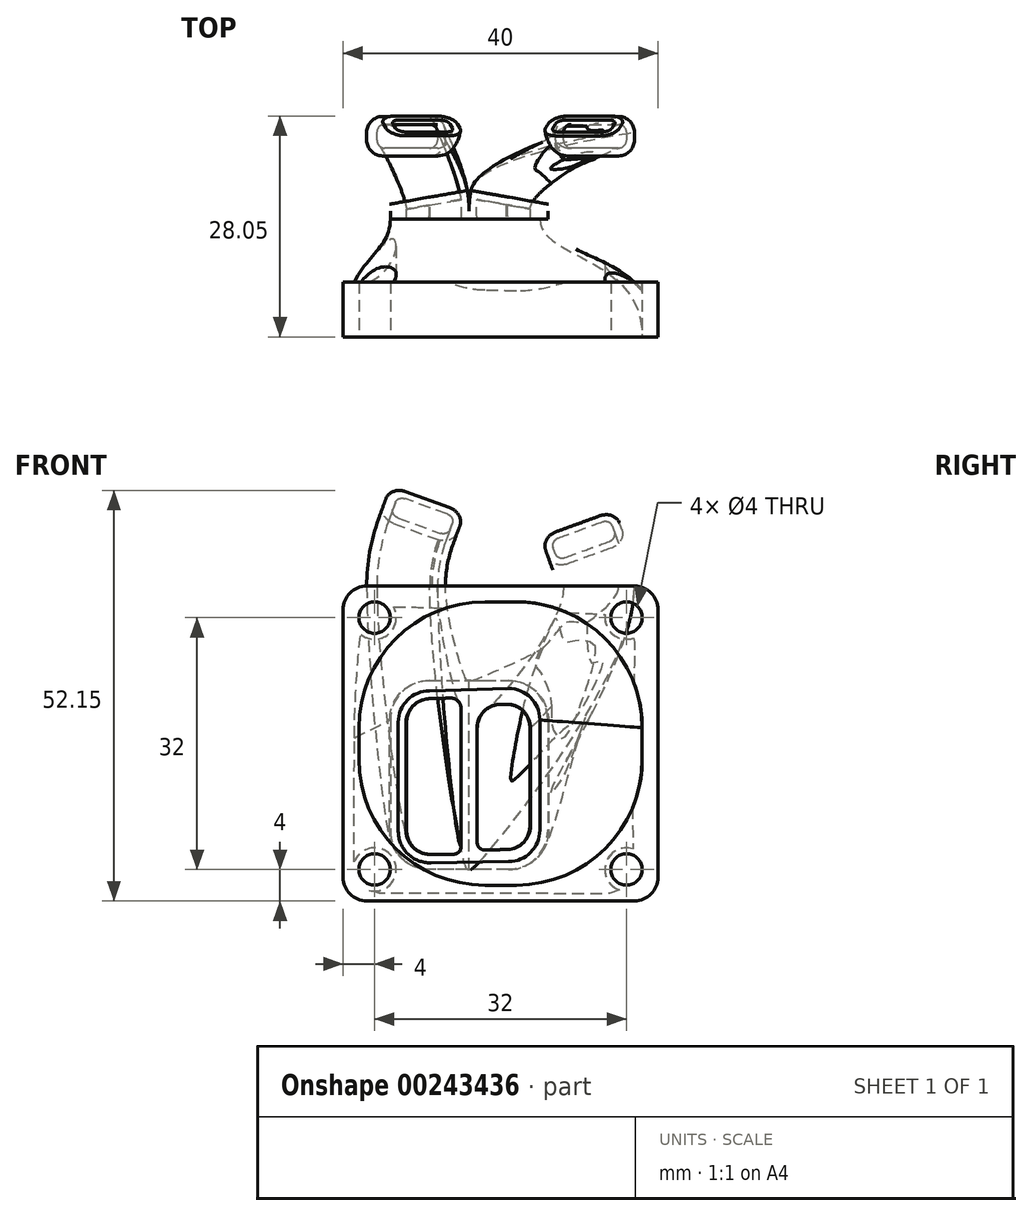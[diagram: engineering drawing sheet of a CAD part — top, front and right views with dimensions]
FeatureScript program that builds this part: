
annotation { "Feature Type Name" : "Feature", "Feature Type Description" : "" }
export const myFeature = defineFeature(function(context is Context, id is Id, definition is map)
    precondition{}
    {
        {
            var Q0;
            Q0=qCreatedBy(makeId("Front.planeOp"),FACE);
            var sketch = newSketch(context, id + "F0", { "sketchPlane" : qUnion([Q0])});
            skLineSegment(sketch, "E0", {"start": v(0, 0) * mm, "end": v(0, 17) * mm});
            skLineSegment(sketch, "E1", {"start": v(3, 20) * mm, "end": v(37, 20) * mm});
            skLineSegment(sketch, "E2", {"start": v(40, 17) * mm, "end": v(40, -17) * mm});
            skLineSegment(sketch, "E3", {"start": v(37, -20) * mm, "end": v(3, -20) * mm});
            skLineSegment(sketch, "E4", {"start": v(0, -17) * mm, "end": v(0, 0) * mm});
            skPoint(sketch, "E5.visualSharp", {"position": v(40, 20) * mm});
            skArc(sketch, "E5.filletArc", {"start": v(40, 17) * mm, "mid": v(39.12, 19.12) * mm, "end": v(37, 20) * mm});
            skPoint(sketch, "E6.visualSharp", {"position": v(40, -20) * mm});
            skArc(sketch, "E6.filletArc", {"start": v(37, -20) * mm, "mid": v(39.12, -19.12) * mm, "end": v(40, -17) * mm});
            skPoint(sketch, "E7.visualSharp", {"position": v(0, -20) * mm});
            skArc(sketch, "E7.filletArc", {"start": v(0, -17) * mm, "mid": v(0.88, -19.12) * mm, "end": v(3, -20) * mm});
            skPoint(sketch, "E8.visualSharp", {"position": v(0, 20) * mm});
            skArc(sketch, "E8.filletArc", {"start": v(3, 20) * mm, "mid": v(0.88, 19.12) * mm, "end": v(0, 17) * mm});
            skSolve(sketch);
        }
        {
            var Q0;
            Q0=qCreatedBy(makeId("Top.planeOp"),FACE);
            cPlane(context, id + "F1", {"entities" : qUnion([Q0]), "cplaneType" : CPlaneType.OFFSET, "offset" : 20 * mm, "width" : 150 * mm, "height" : 150 * mm});
        }
        {
            var Q0;
            Q0=qCreatedBy(id+"F1.planeOp",FACE);
            var sketch = newSketch(context, id + "F2", { "sketchPlane" : qUnion([Q0])});
            skLineSegment(sketch, "E9", {"start": v(3, 26) * mm, "end": v(3, 25) * mm});
            skLineSegment(sketch, "E10", {"start": v(5, 23) * mm, "end": v(11, 23) * mm});
            skLineSegment(sketch, "E11", {"start": v(13, 25) * mm, "end": v(13, 26) * mm});
            skLineSegment(sketch, "E12", {"start": v(37, 26) * mm, "end": v(37, 25) * mm});
            skLineSegment(sketch, "E13", {"start": v(35, 23) * mm, "end": v(29, 23) * mm});
            skLineSegment(sketch, "E14", {"start": v(27, 25) * mm, "end": v(27, 26) * mm});
            skLineSegment(sketch, "E15", {"start": v(5, 28) * mm, "end": v(11, 28) * mm});
            skLineSegment(sketch, "E16", {"start": v(29, 28) * mm, "end": v(35, 28) * mm});
            skPoint(sketch, "E17.visualSharp", {"position": v(13, 28) * mm});
            skArc(sketch, "E17.filletArc", {"start": v(13, 26) * mm, "mid": v(12.41, 27.41) * mm, "end": v(11, 28) * mm});
            skPoint(sketch, "E18.visualSharp", {"position": v(13, 23) * mm});
            skArc(sketch, "E18.filletArc", {"start": v(11, 23) * mm, "mid": v(12.41, 23.59) * mm, "end": v(13, 25) * mm});
            skPoint(sketch, "E19.visualSharp", {"position": v(3, 23) * mm});
            skArc(sketch, "E19.filletArc", {"start": v(3, 25) * mm, "mid": v(3.59, 23.59) * mm, "end": v(5, 23) * mm});
            skPoint(sketch, "E20.visualSharp", {"position": v(3, 28) * mm});
            skArc(sketch, "E20.filletArc", {"start": v(5, 28) * mm, "mid": v(3.59, 27.41) * mm, "end": v(3, 26) * mm});
            skPoint(sketch, "E21.visualSharp", {"position": v(27, 28) * mm});
            skArc(sketch, "E21.filletArc", {"start": v(29, 28) * mm, "mid": v(27.59, 27.41) * mm, "end": v(27, 26) * mm});
            skPoint(sketch, "E22.visualSharp", {"position": v(27, 23) * mm});
            skArc(sketch, "E22.filletArc", {"start": v(27, 25) * mm, "mid": v(27.59, 23.59) * mm, "end": v(29, 23) * mm});
            skPoint(sketch, "E23.visualSharp", {"position": v(37, 23) * mm});
            skArc(sketch, "E23.filletArc", {"start": v(35, 23) * mm, "mid": v(36.41, 23.59) * mm, "end": v(37, 25) * mm});
            skPoint(sketch, "E24.visualSharp", {"position": v(37, 28) * mm});
            skArc(sketch, "E24.filletArc", {"start": v(37, 26) * mm, "mid": v(36.41, 27.41) * mm, "end": v(35, 28) * mm});
            skSolve(sketch);
        }
        {
            var Q0;
            Q0=qCreatedBy(makeId("Front.planeOp"),FACE);
            cPlane(context, id + "F3", {"entities" : qUnion([Q0]), "cplaneType" : CPlaneType.OFFSET, "offset" : 15 * mm, "oppositeDirection" : true, "width" : 150 * mm, "height" : 150 * mm});
        }
        {
            var Q0;
            Q0=qCreatedBy(id+"F3.planeOp",FACE);
            var sketch = newSketch(context, id + "F4", { "sketchPlane" : qUnion([Q0])});
            skLineSegment(sketch, "E25", {"start": v(11, 8) * mm, "end": v(21, 8) * mm});
            skLineSegment(sketch, "E26", {"start": v(26, 3) * mm, "end": v(26, -11) * mm});
            skLineSegment(sketch, "E27", {"start": v(21, -16) * mm, "end": v(11, -16) * mm});
            skLineSegment(sketch, "E28", {"start": v(6, 3) * mm, "end": v(6, -11) * mm});
            skPoint(sketch, "E29.visualSharp", {"position": v(6, 8) * mm});
            skArc(sketch, "E29.filletArc", {"start": v(11, 8) * mm, "mid": v(7.46, 6.54) * mm, "end": v(6, 3) * mm});
            skPoint(sketch, "E30.visualSharp", {"position": v(6, -16) * mm});
            skArc(sketch, "E30.filletArc", {"start": v(6, -11) * mm, "mid": v(7.46, -14.54) * mm, "end": v(11, -16) * mm});
            skPoint(sketch, "E31.visualSharp", {"position": v(26, -16) * mm});
            skArc(sketch, "E31.filletArc", {"start": v(21, -16) * mm, "mid": v(24.54, -14.54) * mm, "end": v(26, -11) * mm});
            skPoint(sketch, "E32.visualSharp", {"position": v(26, 8) * mm});
            skArc(sketch, "E32.filletArc", {"start": v(26, 3) * mm, "mid": v(24.54, 6.54) * mm, "end": v(21, 8) * mm});
            skSolve(sketch);
        }
        {
            var Q0;
            Q0 = qSketchRegion(id + "F0", true);
            var Q1;
            Q1=makeQuery(id+"F4.imprint","IMPRINT",FACE,{"disambiguationData":[TD([[makeQuery(id+"F4.imprint","IMPRINT",EDGE,{"derivedFrom":sQuery(id+"F4.wireOp",EDGE,"E25")}),-1.0]])]});
            loft(context, id + "F5", {"startCondition" : LoftEndDerivativeType.NORMAL_TO_PROFILE, "startMagnitude" : 2, "endCondition" : LoftEndDerivativeType.NORMAL_TO_PROFILE, "endMagnitude" : 1, "sheetProfilesArray" : [{ "sheetProfileEntities" : qUnion([Q0]) }, { "sheetProfileEntities" : qUnion([Q1]) }]});
        }
        {
            var Q0;
            Q0=makeQuery(id+"F5.opLoft","CAP_FACE",FACE,{"disambiguationData":[OSD([makeQuery(id+"F4.imprint","IMPRINT",FACE,{"disambiguationData":[TD([[makeQuery(id+"F4.imprint","IMPRINT",EDGE,{"derivedFrom":sQuery(id+"F4.wireOp",EDGE,"E25")}),-1.0]])]})])],"isStart":true});
            extrude(context, id + "F6", {"entities" : qUnion([Q0]), "operationType" : NewBodyOperationType.ADD, "depth" : 1 * mm});
        }
        {
            var Q0;
            Q0=makeQuery(id+"F6.opExtrude","CAP_FACE",FACE,{"disambiguationData":[OSD([makeQuery(id+"F4.imprint","IMPRINT",FACE,{"disambiguationData":[TD([[makeQuery(id+"F4.imprint","IMPRINT",EDGE,{"derivedFrom":sQuery(id+"F4.wireOp",EDGE,"E25")}),-1.0]])]})])],"isStart":false});
            var sketch = newSketch(context, id + "F7", { "sketchPlane" : qUnion([Q0])});
            skLineSegment(sketch, "E33", {"start": v(-16, -16) * mm, "end": v(-16, 8) * mm});
            skLineSegment(sketch, "E34", {"start": v(-16, 8) * mm, "end": v(-16, 5) * mm});
            skLineSegment(sketch, "E35", {"start": v(-16, 8) * mm, "end": v(-17.5, 8) * mm});
            skLineSegment(sketch, "E36", {"start": v(-16, -16) * mm, "end": v(-16, -13) * mm});
            skLineSegment(sketch, "E37", {"start": v(-16, -16) * mm, "end": v(-17.75, -16) * mm});
            skLineSegment(sketch, "E38", {"start": v(-6, -11) * mm, "end": v(-6, 3) * mm});
            skLineSegment(sketch, "E39", {"start": v(-16, -16) * mm, "end": v(-11, -16) * mm});
            skLineSegment(sketch, "E40", {"start": v(-11, 8) * mm, "end": v(-16, 8) * mm});
            skPoint(sketch, "E41.visualSharp", {"position": v(-6, 8) * mm});
            skArc(sketch, "E41.filletArc", {"start": v(-6, 3) * mm, "mid": v(-7.46, 6.54) * mm, "end": v(-11, 8) * mm});
            skPoint(sketch, "E42.visualSharp", {"position": v(-6, -16) * mm});
            skArc(sketch, "E42.filletArc", {"start": v(-11, -16) * mm, "mid": v(-7.46, -14.54) * mm, "end": v(-6, -11) * mm});
            skLineSegment(sketch, "E43", {"start": v(-11, -16) * mm, "end": v(-14.95, -16) * mm});
            skLineSegment(sketch, "E44", {"start": v(-14.95, -16) * mm, "end": v(-16, -16) * mm});
            skLineSegment(sketch, "E45", {"start": v(-11, 8) * mm, "end": v(-14.63, 8) * mm});
            skLineSegment(sketch, "E46", {"start": v(-14.63, 8) * mm, "end": v(-16, 8) * mm});
            skSolve(sketch);
        }
        {
            var Q0;
            Q0=makeQuery(id+"F7.imprint","IMPRINT",FACE,{"disambiguationData":[TD([[makeQuery(id+"F7.imprint","IMPRINT",EDGE,{"derivedFrom":sQuery(id+"F7.wireOp",EDGE,"E33")}),-1.0]])]});
            var sketch = newSketch(context, id + "F8", { "sketchPlane" : qUnion([Q0])});
            skLineSegment(sketch, "E47", {"start": v(-1, -4.8) * mm, "end": v(-1, 5.62) * mm});
            skLineSegment(sketch, "E48", {"start": v(-31, 5.62) * mm, "end": v(-31, -15.15) * mm});
            skSolve(sketch);
        }
        {
            var Q0;
            Q0=makeQuery(id+"F7.imprint","IMPRINT",FACE,{"disambiguationData":[TD([[makeQuery(id+"F7.imprint","IMPRINT",EDGE,{"derivedFrom":sQuery(id+"F7.wireOp",EDGE,"E33")}),1.0]])]});
            var Q1;
            Q1=sQuery(id+"F8.wireOp",EDGE,"E48");
            revolve(context, id + "F9", {"operationType" : NewBodyOperationType.ADD, "entities" : qUnion([Q0]), "axis" : qUnion([Q1]), "revolveType" : RevolveType.ONE_DIRECTION, "angle" : 10 * degree});
        }
        {
            var Q0;
            Q0=makeQuery(id+"F7.imprint","IMPRINT",FACE,{"disambiguationData":[TD([[makeQuery(id+"F7.imprint","IMPRINT",EDGE,{"derivedFrom":sQuery(id+"F7.wireOp",EDGE,"E33")}),-1.0]])]});
            var Q1;
            Q1=sQuery(id+"F8.wireOp",EDGE,"E47");
            revolve(context, id + "F10", {"operationType" : NewBodyOperationType.ADD, "entities" : qUnion([Q0]), "axis" : qUnion([Q1]), "revolveType" : RevolveType.ONE_DIRECTION, "angle" : 10 * degree});
        }
        {
            var Q1;
            Q1=makeQuery(id+"F9.opRevolve","CAP_FACE",FACE,{"disambiguationData":[OSD([sQuery(id+"F4.wireOp",EDGE,"E25"),sQuery(id+"F4.wireOp",EDGE,"E26"),sQuery(id+"F4.wireOp",EDGE,"E27"),sQuery(id+"F4.wireOp",EDGE,"E29.filletArc"),sQuery(id+"F4.wireOp",EDGE,"E30.filletArc"),sQuery(id+"F4.wireOp",EDGE,"E31.filletArc"),sQuery(id+"F4.wireOp",EDGE,"E32.filletArc"),sQuery(id+"F7.wireOp",EDGE,"E33"),sQuery(id+"F7.wireOp",EDGE,"E34"),sQuery(id+"F7.wireOp",EDGE,"E35"),sQuery(id+"F7.wireOp",EDGE,"E36"),sQuery(id+"F7.wireOp",EDGE,"E37")])],"isStart":false});
            var Q2;
            Q2=makeQuery(id+"F2.imprint","IMPRINT",FACE,{"disambiguationData":[TD([[makeQuery(id+"F2.imprint","IMPRINT",EDGE,{"derivedFrom":sQuery(id+"F2.wireOp",EDGE,"E12")}),-1.0]])]});
            loft(context, id + "F11", {"operationType" : NewBodyOperationType.ADD, "startCondition" : LoftEndDerivativeType.NORMAL_TO_PROFILE, "startMagnitude" : 1, "endCondition" : LoftEndDerivativeType.NORMAL_TO_PROFILE, "endMagnitude" : 1, "sheetProfilesArray" : [{ "sheetProfileEntities" : qUnion([Q1]) }, { "sheetProfileEntities" : qUnion([Q2]) }]});
        }
        {
            var Q1;
            Q1=makeQuery(id+"F10.opRevolve","CAP_FACE",FACE,{"disambiguationData":[OSD([sQuery(id+"F0.wireOp",EDGE,"E0"),sQuery(id+"F0.wireOp",EDGE,"E4"),sQuery(id+"F4.wireOp",EDGE,"E25"),sQuery(id+"F4.wireOp",EDGE,"E27"),sQuery(id+"F4.wireOp",EDGE,"E28"),sQuery(id+"F4.wireOp",EDGE,"E29.filletArc"),sQuery(id+"F4.wireOp",EDGE,"E30.filletArc"),sQuery(id+"F4.wireOp",EDGE,"E31.filletArc"),sQuery(id+"F4.wireOp",EDGE,"E32.filletArc"),sQuery(id+"F7.wireOp",EDGE,"E33"),sQuery(id+"F7.wireOp",EDGE,"eooe6Qcx-zl0v-XeAy-R2di-PJaWR5bL0I77"),sQuery(id+"F7.wireOp",EDGE,"E34"),sQuery(id+"F7.wireOp",EDGE,"E36"),sQuery(id+"F7.wireOp",EDGE,"KL9OZESf-6kgJ-Yt0d-4tDR-3qCoX2jgUDdf")])],"isStart":false});
            var Q2;
            Q2=makeQuery(id+"F2.imprint","IMPRINT",FACE,{"disambiguationData":[TD([[makeQuery(id+"F2.imprint","IMPRINT",EDGE,{"derivedFrom":sQuery(id+"F2.wireOp",EDGE,"E9")}),1.0]])]});
            var Q3;
            Q3=makeQuery(id+"F10.opRevolve","CAP_VERTEX",VERTEX,{"disambiguationData":[OSD([sQuery(id+"F7.wireOp",EDGE,"E34"),sQuery(id+"F7.wireOp",EDGE,"E35"),sQuery(id+"F7.wireOp",EDGE,"E46")])],"isStart":false});
            var Q4;
            Q4=sQuery(id+"F2.wireOp",VERTEX,"E11.start");
            loft(context, id + "F12", {"operationType" : NewBodyOperationType.ADD, "startCondition" : LoftEndDerivativeType.NORMAL_TO_PROFILE, "startMagnitude" : 1, "endCondition" : LoftEndDerivativeType.NORMAL_TO_PROFILE, "endMagnitude" : 1, "sheetProfilesArray" : [{ "sheetProfileEntities" : qUnion([Q1]) }, { "sheetProfileEntities" : qUnion([Q2]) }], "matchConnections" : true, "connections" : [{ "connectionEntities" : qUnion([Q3, Q4]), "connectionEdgeQueries" : qUnion([]), "connectionEdgeParameters" : [] }]});
        }
        {
            var Q0;
            Q0=makeQuery(id+"F2.imprint","IMPRINT",FACE,{"disambiguationData":[TD([[makeQuery(id+"F2.imprint","IMPRINT",EDGE,{"derivedFrom":sQuery(id+"F2.wireOp",EDGE,"E9")}),1.0]])]});
            var sketch = newSketch(context, id + "F13", { "sketchPlane" : qUnion([Q0])});
            skLineSegment(sketch, "E49", {"start": v(12, 26) * mm, "end": v(12, 25) * mm});
            skLineSegment(sketch, "E50", {"start": v(11, 24) * mm, "end": v(5.3, 24) * mm});
            skLineSegment(sketch, "E51", {"start": v(4.3, 25) * mm, "end": v(4.3, 26) * mm});
            skLineSegment(sketch, "E52", {"start": v(5.3, 27) * mm, "end": v(11, 27) * mm});
            skPoint(sketch, "E53.visualSharp", {"position": v(4.3, 27) * mm});
            skArc(sketch, "E53.filletArc", {"start": v(5.3, 27) * mm, "mid": v(4.58, 26.7) * mm, "end": v(4.3, 26) * mm});
            skPoint(sketch, "E54.visualSharp", {"position": v(4.3, 24) * mm});
            skArc(sketch, "E54.filletArc", {"start": v(4.3, 25) * mm, "mid": v(4.58, 24.3) * mm, "end": v(5.3, 24) * mm});
            skPoint(sketch, "E55.visualSharp", {"position": v(12, 27) * mm});
            skArc(sketch, "E55.filletArc", {"start": v(12, 26) * mm, "mid": v(11.7, 26.7) * mm, "end": v(11, 27) * mm});
            skPoint(sketch, "E56.visualSharp", {"position": v(12, 24) * mm});
            skArc(sketch, "E56.filletArc", {"start": v(11, 24) * mm, "mid": v(11.7, 24.3) * mm, "end": v(12, 25) * mm});
            skLineSegment(sketch, "E57", {"start": v(36, 26) * mm, "end": v(36, 25) * mm});
            skLineSegment(sketch, "E58", {"start": v(35, 24) * mm, "end": v(29, 24) * mm});
            skLineSegment(sketch, "E59", {"start": v(28, 25) * mm, "end": v(28, 26) * mm});
            skLineSegment(sketch, "E60", {"start": v(29, 27) * mm, "end": v(35, 27) * mm});
            skPoint(sketch, "E61.visualSharp", {"position": v(28, 27) * mm});
            skArc(sketch, "E61.filletArc", {"start": v(29, 27) * mm, "mid": v(28.3, 26.7) * mm, "end": v(28, 26) * mm});
            skPoint(sketch, "E62.visualSharp", {"position": v(28, 24) * mm});
            skArc(sketch, "E62.filletArc", {"start": v(28, 25) * mm, "mid": v(28.3, 24.3) * mm, "end": v(29, 24) * mm});
            skPoint(sketch, "E63.visualSharp", {"position": v(36, 24) * mm});
            skArc(sketch, "E63.filletArc", {"start": v(35, 24) * mm, "mid": v(35.7, 24.3) * mm, "end": v(36, 25) * mm});
            skPoint(sketch, "E64.visualSharp", {"position": v(36, 27) * mm});
            skArc(sketch, "E64.filletArc", {"start": v(36, 26) * mm, "mid": v(35.7, 26.7) * mm, "end": v(35, 27) * mm});
            skSolve(sketch);
        }
        {
            var Q0;
            Q0=makeQuery(id+"F0.imprint","IMPRINT",FACE,{"disambiguationData":[TD([[makeQuery(id+"F0.imprint","IMPRINT",EDGE,{"derivedFrom":sQuery(id+"F0.wireOp",EDGE,"E0")}),-1.0]])]});
            var sketch = newSketch(context, id + "F14", { "sketchPlane" : qUnion([Q0])});
            skLineSegment(sketch, "E65", {"start": v(22, -18) * mm, "end": v(18, -18) * mm});
            skLineSegment(sketch, "E66", {"start": v(2, -2) * mm, "end": v(2, 2) * mm});
            skLineSegment(sketch, "E67", {"start": v(38, -2) * mm, "end": v(38, 2) * mm});
            skLineSegment(sketch, "E68", {"start": v(22, 18) * mm, "end": v(18, 18) * mm});
            skPoint(sketch, "E69.visualSharp", {"position": v(2, -18) * mm});
            skArc(sketch, "E69.filletArc", {"start": v(2, -2) * mm, "mid": v(6.69, -13.31) * mm, "end": v(18, -18) * mm});
            skPoint(sketch, "E70.visualSharp", {"position": v(2, 18) * mm});
            skArc(sketch, "E70.filletArc", {"start": v(18, 18) * mm, "mid": v(6.69, 13.31) * mm, "end": v(2, 2) * mm});
            skPoint(sketch, "E71.visualSharp", {"position": v(38, 18) * mm});
            skArc(sketch, "E71.filletArc", {"start": v(38, 2) * mm, "mid": v(33.31, 13.31) * mm, "end": v(22, 18) * mm});
            skPoint(sketch, "E72.visualSharp", {"position": v(38, -18) * mm});
            skArc(sketch, "E72.filletArc", {"start": v(22, -18) * mm, "mid": v(33.31, -13.31) * mm, "end": v(38, -2) * mm});
            skSolve(sketch);
        }
        {
            var Q0;
            Q0=qCreatedBy(id+"F3.planeOp",FACE);
            var sketch = newSketch(context, id + "F15", { "sketchPlane" : qUnion([Q0])});
            skLineSegment(sketch, "E73", {"start": v(25, 3) * mm, "end": v(25, -11) * mm});
            skLineSegment(sketch, "E74", {"start": v(7, -11.15) * mm, "end": v(7, 2.7) * mm});
            skPoint(sketch, "E75.visualSharp", {"position": v(25, -15) * mm});
            skArc(sketch, "E75.filletArc", {"start": v(21, -15) * mm, "mid": v(23.83, -13.83) * mm, "end": v(25, -11) * mm});
            skPoint(sketch, "E76.visualSharp", {"position": v(25, 7) * mm});
            skArc(sketch, "E76.filletArc", {"start": v(25, 3) * mm, "mid": v(23.83, 5.83) * mm, "end": v(21, 7) * mm});
            skPoint(sketch, "E77.visualSharp", {"position": v(7, 6.7) * mm});
            skArc(sketch, "E77.filletArc", {"start": v(11, 6.7) * mm, "mid": v(8.18, 5.53) * mm, "end": v(7, 2.7) * mm});
            skPoint(sketch, "E78.visualSharp", {"position": v(7, -15.3) * mm});
            skArc(sketch, "E78.filletArc", {"start": v(7, -11.15) * mm, "mid": v(8.23, -14.03) * mm, "end": v(11.16, -15.14) * mm});
            skLineSegment(sketch, "E79", {"start": v(21, -15) * mm, "end": v(11.16, -15.14) * mm});
            skLineSegment(sketch, "E80", {"start": v(11, 6.7) * mm, "end": v(21, 7) * mm});
            skSolve(sketch);
        }
        {
            var Q1;
            Q1 = qSketchRegion(id + "F15", true);
            var Q2;
            Q2 = qSketchRegion(id + "F14", true);
            loft(context, id + "F16", {"operationType" : NewBodyOperationType.REMOVE, "startCondition" : LoftEndDerivativeType.NORMAL_TO_PROFILE, "startMagnitude" : 1, "endCondition" : LoftEndDerivativeType.NORMAL_TO_PROFILE, "endMagnitude" : 2, "sheetProfilesArray" : [{ "sheetProfileEntities" : qUnion([Q1]) }, { "sheetProfileEntities" : qUnion([Q2]) }]});
        }
        {
            var Q0;
            Q0=qCreatedBy(id+"F3.planeOp",FACE);
            var sketch = newSketch(context, id + "F17", { "sketchPlane" : qUnion([Q0])});
            skLineSegment(sketch, "E81", {"start": v(8, -11.07) * mm, "end": v(8, 2.7) * mm});
            skLineSegment(sketch, "E82", {"start": v(10.92, 5.7) * mm, "end": v(13.66, 5.78) * mm});
            skLineSegment(sketch, "E83", {"start": v(11, -14.07) * mm, "end": v(14, -14.07) * mm});
            skPoint(sketch, "E84.visualSharp", {"position": v(8, 5.6) * mm});
            skArc(sketch, "E84.filletArc", {"start": v(10.92, 5.7) * mm, "mid": v(8.85, 4.79) * mm, "end": v(8, 2.7) * mm});
            skPoint(sketch, "E85.visualSharp", {"position": v(24, 6.24) * mm});
            skPoint(sketch, "E86.visualSharp", {"position": v(24, -14.07) * mm});
            skPoint(sketch, "E87.visualSharp", {"position": v(8, -14.07) * mm});
            skArc(sketch, "E87.filletArc", {"start": v(8, -11.07) * mm, "mid": v(8.88, -13.2) * mm, "end": v(11, -14.07) * mm});
            skLineSegment(sketch, "E88", {"start": v(15, 4.48) * mm, "end": v(15, -13.07) * mm});
            skPoint(sketch, "E89.visualSharp", {"position": v(15, 5.82) * mm});
            skArc(sketch, "E89.filletArc", {"start": v(15, 4.48) * mm, "mid": v(14.6, 5.41) * mm, "end": v(13.66, 5.78) * mm});
            skPoint(sketch, "E90.visualSharp", {"position": v(15, -14.07) * mm});
            skArc(sketch, "E90.filletArc", {"start": v(14, -14.07) * mm, "mid": v(14.71, -13.78) * mm, "end": v(15, -13.07) * mm});
            skSolve(sketch);
        }
        {
            var Q0;
            Q0=qCreatedBy(id+"F3.planeOp",FACE);
            var sketch = newSketch(context, id + "F18", { "sketchPlane" : qUnion([Q0])});
            skLineSegment(sketch, "E91", {"start": v(23.8, 2) * mm, "end": v(23.8, -10.46) * mm});
            skLineSegment(sketch, "E92", {"start": v(20.88, -13.46) * mm, "end": v(18.03, -13.53) * mm});
            skLineSegment(sketch, "E93", {"start": v(17, -12.54) * mm, "end": v(17, 1.97) * mm});
            skLineSegment(sketch, "E94", {"start": v(19.92, 4.97) * mm, "end": v(20.72, 5) * mm});
            skPoint(sketch, "E95.visualSharp", {"position": v(17, -13.56) * mm});
            skArc(sketch, "E95.filletArc", {"start": v(17, -12.54) * mm, "mid": v(17.3, -13.25) * mm, "end": v(18.03, -13.53) * mm});
            skPoint(sketch, "E96.visualSharp", {"position": v(17, 4.9) * mm});
            skArc(sketch, "E96.filletArc", {"start": v(19.92, 4.97) * mm, "mid": v(17.85, 4.06) * mm, "end": v(17, 1.97) * mm});
            skPoint(sketch, "E97.visualSharp", {"position": v(23.8, 5.08) * mm});
            skArc(sketch, "E97.filletArc", {"start": v(23.8, 2) * mm, "mid": v(22.9, 4.14) * mm, "end": v(20.72, 5) * mm});
            skPoint(sketch, "E98.visualSharp", {"position": v(23.8, -13.38) * mm});
            skArc(sketch, "E98.filletArc", {"start": v(20.88, -13.46) * mm, "mid": v(22.95, -12.55) * mm, "end": v(23.8, -10.46) * mm});
            skSolve(sketch);
        }
        {
            var Q0;
            Q0 = qSketchRegion(id + "F17", true);
            var Q1;
            Q1=sQuery(id+"F8.wireOp",EDGE,"E47");
            revolve(context, id + "F19", {"operationType" : NewBodyOperationType.REMOVE, "entities" : qUnion([Q0]), "axis" : qUnion([Q1]), "revolveType" : RevolveType.ONE_DIRECTION, "angle" : 10 * degree});
        }
        {
            var Q0;
            Q0 = qSketchRegion(id + "F18", true);
            var Q1;
            Q1=sQuery(id+"F8.wireOp",EDGE,"E48");
            revolve(context, id + "F20", {"operationType" : NewBodyOperationType.REMOVE, "entities" : qUnion([Q0]), "axis" : qUnion([Q1]), "revolveType" : RevolveType.ONE_DIRECTION, "angle" : 10 * degree});
        }
        {
            var Q1;
            Q1=makeQuery(id+"F20.boolean.opBoolean","COPY",FACE,{"derivedFrom":makeQuery(id+"F20.opRevolve","CAP_FACE",FACE,{"disambiguationData":[OSD([sQuery(id+"F18.wireOp",EDGE,"E91"),sQuery(id+"F18.wireOp",EDGE,"E92"),sQuery(id+"F18.wireOp",EDGE,"E93"),sQuery(id+"F18.wireOp",EDGE,"E94"),sQuery(id+"F18.wireOp",EDGE,"E95.filletArc"),sQuery(id+"F18.wireOp",EDGE,"E96.filletArc"),sQuery(id+"F18.wireOp",EDGE,"E97.filletArc"),sQuery(id+"F18.wireOp",EDGE,"E98.filletArc")])],"isStart":false})});
            var Q2;
            Q2=makeQuery(id+"F13.imprint","IMPRINT",FACE,{"disambiguationData":[TD([[makeQuery(id+"F13.imprint","IMPRINT",EDGE,{"derivedFrom":sQuery(id+"F13.wireOp",EDGE,"E57")}),-1.0]])]});
            loft(context, id + "F21", {"operationType" : NewBodyOperationType.REMOVE, "startCondition" : LoftEndDerivativeType.NORMAL_TO_PROFILE, "startMagnitude" : 1, "endCondition" : LoftEndDerivativeType.NORMAL_TO_PROFILE, "endMagnitude" : 1, "sheetProfilesArray" : [{ "sheetProfileEntities" : qUnion([Q1]) }, { "sheetProfileEntities" : qUnion([Q2]) }]});
        }
        {
            var Q1;
            Q1=makeQuery(id+"F13.imprint","IMPRINT",FACE,{"disambiguationData":[TD([[makeQuery(id+"F13.imprint","IMPRINT",EDGE,{"derivedFrom":sQuery(id+"F13.wireOp",EDGE,"E49")}),-1.0]])]});
            var Q2;
            Q2=makeQuery(id+"F19.boolean.opBoolean","COPY",FACE,{"derivedFrom":makeQuery(id+"F19.opRevolve","CAP_FACE",FACE,{"disambiguationData":[OSD([sQuery(id+"F17.wireOp",EDGE,"E81"),sQuery(id+"F17.wireOp",EDGE,"E82"),sQuery(id+"F17.wireOp",EDGE,"E83"),sQuery(id+"F17.wireOp",EDGE,"E84.filletArc"),sQuery(id+"F17.wireOp",EDGE,"E87.filletArc"),sQuery(id+"F17.wireOp",EDGE,"E88"),sQuery(id+"F17.wireOp",EDGE,"E89.filletArc"),sQuery(id+"F17.wireOp",EDGE,"E90.filletArc")])],"isStart":false})});
            loft(context, id + "F22", {"operationType" : NewBodyOperationType.REMOVE, "startCondition" : LoftEndDerivativeType.NORMAL_TO_PROFILE, "startMagnitude" : 1, "endCondition" : LoftEndDerivativeType.NORMAL_TO_PROFILE, "endMagnitude" : 1, "sheetProfilesArray" : [{ "sheetProfileEntities" : qUnion([Q1]) }, { "sheetProfileEntities" : qUnion([Q2]) }]});
        }
        {
            var Q0;
            Q0=makeQuery(id+"F13.imprint","IMPRINT",FACE,{"disambiguationData":[TD([[makeQuery(id+"F13.imprint","IMPRINT",EDGE,{"derivedFrom":sQuery(id+"F13.wireOp",EDGE,"E49")}),1.0]])]});
            var sketch = newSketch(context, id + "F23", { "sketchPlane" : qUnion([Q0])});
            skLineSegment(sketch, "E99", {"start": v(11, 27.98) * mm, "end": v(29, 27.98) * mm});
            skLineSegment(sketch, "E100", {"start": v(11, 27.98) * mm, "end": v(11, 32.98) * mm});
            skLineSegment(sketch, "E101", {"start": v(29, 27.98) * mm, "end": v(29, 32.98) * mm});
            skLineSegment(sketch, "E102", {"start": v(29, 32.98) * mm, "end": v(20, 27.98) * mm});
            skLineSegment(sketch, "E103", {"start": v(20, 27.98) * mm, "end": v(11, 32.98) * mm});
            skLineSegment(sketch, "E104", {"start": v(21, 27.98) * mm, "end": v(21, 22.98) * mm});
            skSolve(sketch);
        }
        {
            var Q0;
            Q0=makeQuery(id+"F5.opLoft","CAP_FACE",FACE,{"disambiguationData":[OSD([makeQuery(id+"F0.imprint","IMPRINT",FACE,{"disambiguationData":[TD([[makeQuery(id+"F0.imprint","IMPRINT",EDGE,{"derivedFrom":sQuery(id+"F0.wireOp",EDGE,"E0")}),-1.0]])]})])],"isStart":true});
            var sketch = newSketch(context, id + "F24", { "sketchPlane" : qUnion([Q0])});
            skCircle(sketch, "E105", {"center": v(4, 16) * mm, "radius": 2 * mm});
            skCircle(sketch, "E106", {"center": v(36, 16) * mm, "radius": 2 * mm});
            skCircle(sketch, "E107", {"center": v(36, -16) * mm, "radius": 2 * mm});
            skCircle(sketch, "E108", {"center": v(4, -16) * mm, "radius": 2 * mm});
            skSolve(sketch);
        }
        {
            var Q0;
            Q0=makeQuery(id+"F24.imprint","IMPRINT",FACE,{"disambiguationData":[TD([[makeQuery(id+"F24.imprint","IMPRINT",EDGE,{"derivedFrom":sQuery(id+"F24.wireOp",EDGE,"E105")}),-1.0]])]});
            extrude(context, id + "F25", {"entities" : qUnion([Q0]), "operationType" : NewBodyOperationType.ADD, "oppositeDirection" : true, "depth" : 7 * mm});
        }
        {
            var Q0;
            Q0=makeQuery(id+"F24.imprint","IMPRINT",FACE,{"disambiguationData":[TD([[makeQuery(id+"F24.imprint","IMPRINT",EDGE,{"derivedFrom":sQuery(id+"F24.wireOp",EDGE,"E105")}),1.0]])]});
            var Q1;
            Q1=makeQuery(id+"F24.imprint","IMPRINT",FACE,{"disambiguationData":[TD([[makeQuery(id+"F24.imprint","IMPRINT",EDGE,{"derivedFrom":sQuery(id+"F24.wireOp",EDGE,"E106")}),1.0]])]});
            var Q2;
            Q2=makeQuery(id+"F24.imprint","IMPRINT",FACE,{"disambiguationData":[TD([[makeQuery(id+"F24.imprint","IMPRINT",EDGE,{"derivedFrom":sQuery(id+"F24.wireOp",EDGE,"E107")}),1.0]])]});
            var Q3;
            Q3=makeQuery(id+"F24.imprint","IMPRINT",FACE,{"disambiguationData":[TD([[makeQuery(id+"F24.imprint","IMPRINT",EDGE,{"derivedFrom":sQuery(id+"F24.wireOp",EDGE,"E108")}),1.0]])]});
            var Q4;
            Q4=sQuery(id+"F24.wireOp",EDGE,"E105");
            var Q5;
            Q5=sQuery(id+"F24.wireOp",EDGE,"E106");
            var Q6;
            Q6=sQuery(id+"F24.wireOp",EDGE,"E107");
            var Q7;
            Q7=sQuery(id+"F24.wireOp",EDGE,"E108");
            extrude(context, id + "F26", {"entities" : qUnion([Q0, Q1, Q2, Q3]), "operationType" : NewBodyOperationType.REMOVE, "surfaceEntities" : qUnion([Q4, Q5, Q6, Q7]), "oppositeDirection" : true, "depth" : 15 * mm});
        }
        {
            var Q0;
            Q0=makeQuery(id+"F25.opExtrude","CAP_FACE",FACE,{"disambiguationData":[OSD([sQuery(id+"F0.wireOp",EDGE,"E0"),sQuery(id+"F0.wireOp",EDGE,"E1"),sQuery(id+"F0.wireOp",EDGE,"E2"),sQuery(id+"F0.wireOp",EDGE,"E3"),sQuery(id+"F0.wireOp",EDGE,"E4"),sQuery(id+"F0.wireOp",EDGE,"E5.filletArc"),sQuery(id+"F0.wireOp",EDGE,"E6.filletArc"),sQuery(id+"F0.wireOp",EDGE,"E7.filletArc"),sQuery(id+"F0.wireOp",EDGE,"E8.filletArc"),sQuery(id+"F14.wireOp",EDGE,"E65"),sQuery(id+"F14.wireOp",EDGE,"E66"),sQuery(id+"F14.wireOp",EDGE,"E67"),sQuery(id+"F14.wireOp",EDGE,"E68"),sQuery(id+"F14.wireOp",EDGE,"E69.filletArc"),sQuery(id+"F14.wireOp",EDGE,"E70.filletArc"),sQuery(id+"F14.wireOp",EDGE,"E71.filletArc"),sQuery(id+"F14.wireOp",EDGE,"E72.filletArc"),sQuery(id+"F24.wireOp",EDGE,"E105"),sQuery(id+"F24.wireOp",EDGE,"E106"),sQuery(id+"F24.wireOp",EDGE,"E107"),sQuery(id+"F24.wireOp",EDGE,"E108")])],"isStart":false});
            var sketch = newSketch(context, id + "F27", { "sketchPlane" : qUnion([Q0])});
            skCircle(sketch, "E109", {"center": v(-36, -16) * mm, "radius": 2.75 * mm});
            skLineSegment(sketch, "E110", {"start": v(-36, -16) * mm, "end": v(-4, -16) * mm});
            skCircle(sketch, "E111", {"center": v(-36, 16) * mm, "radius": 2.75 * mm});
            skCircle(sketch, "E112", {"center": v(-4, 16) * mm, "radius": 2.75 * mm});
            skCircle(sketch, "E113", {"center": v(-4, -16) * mm, "radius": 2.75 * mm});
            skSolve(sketch);
        }
        {
            var Q0;
            {var subQ1=sQuery(id+"F24.wireOp",EDGE,"E105");var subQ11=makeQuery(id+"F25.opExtrude","CAP_EDGE",EDGE,{"disambiguationData":[OSD([subQ1])],"isStart":false});Q0=makeQuery(id+"F27.imprint","IMPRINT",FACE,{"disambiguationData":[TD([[makeQuery(id+"F27.imprint","IMPRINT",EDGE,{"derivedFrom":subQ11}),-1.0]])]});}
            var Q1;
            {var subQ0=sQuery(id+"F27.wireOp",EDGE,"E113");var subQ1=makeQuery(id+"F27.imprint","INTERSECT",VERTEX,{"derivedFrom":[sQuery(id+"F27.wireOp",EDGE,"E110"),subQ0]});Q1=makeQuery(id+"F27.imprint","IMPRINT",FACE,{"disambiguationData":[TD([[makeQuery(id+"F27.imprint","IMPRINT",EDGE,{"disambiguationData":[TD([[subQ1,1.0]])],"derivedFrom":subQ0}),1.0]])]});}
            var Q2;
            {var subQ0=sQuery(id+"F24.wireOp",EDGE,"E107");var subQ7=makeQuery(id+"F25.opExtrude","CAP_EDGE",EDGE,{"disambiguationData":[OSD([subQ0])],"isStart":false});Q2=makeQuery(id+"F27.imprint","IMPRINT",FACE,{"disambiguationData":[TD([[makeQuery(id+"F27.imprint","IMPRINT",EDGE,{"derivedFrom":subQ7}),-1.0]])]});}
            var Q3;
            {var subQ1=sQuery(id+"F24.wireOp",EDGE,"E106");var subQ11=makeQuery(id+"F25.opExtrude","CAP_EDGE",EDGE,{"disambiguationData":[OSD([subQ1])],"isStart":false});Q3=makeQuery(id+"F27.imprint","IMPRINT",FACE,{"disambiguationData":[TD([[makeQuery(id+"F27.imprint","IMPRINT",EDGE,{"derivedFrom":subQ11}),-1.0]])]});}
            extrude(context, id + "F28", {"entities" : qUnion([Q0, Q1, Q2, Q3]), "operationType" : NewBodyOperationType.REMOVE, "depth" : 6 * mm});
        }
        {
            var Q0;
            Q0=makeQuery(id+"F23.imprint","IMPRINT",FACE,{"disambiguationData":[TD([[makeQuery(id+"F23.imprint","IMPRINT",EDGE,{"derivedFrom":makeQuery(id+"F13.imprint","IMPRINT",EDGE,{"derivedFrom":sQuery(id+"F13.wireOp",EDGE,"E49")})}),1.0]])]});
            var Q1;
            Q1=sQuery(id+"F13.wireOp",EDGE,"E59");
            revolve(context, id + "F29", {"operationType" : NewBodyOperationType.ADD, "entities" : qUnion([Q0]), "axis" : qUnion([Q1]), "revolveType" : RevolveType.ONE_DIRECTION, "angle" : 20 * degree});
        }
        {
            var Q0;
            Q0=makeQuery(id+"F11.opLoft","CAP_FACE",FACE,{"disambiguationData":[OSD([makeQuery(id+"F2.imprint","IMPRINT",FACE,{"disambiguationData":[TD([[makeQuery(id+"F2.imprint","IMPRINT",EDGE,{"derivedFrom":sQuery(id+"F2.wireOp",EDGE,"E12")}),-1.0]])]})])],"isStart":true});
            var Q1;
            Q1=sQuery(id+"F23.wireOp",EDGE,"E104");
            revolve(context, id + "F30", {"operationType" : NewBodyOperationType.ADD, "entities" : qUnion([Q0]), "axis" : qUnion([Q1]), "revolveType" : RevolveType.ONE_DIRECTION, "angle" : 20 * degree});
        }
        {
            var Q0;
            Q0=makeQuery(id+"F29.opRevolve","CAP_FACE",FACE,{"disambiguationData":[OSD([sQuery(id+"F2.wireOp",EDGE,"E9"),sQuery(id+"F2.wireOp",EDGE,"E10"),sQuery(id+"F2.wireOp",EDGE,"E11"),sQuery(id+"F2.wireOp",EDGE,"E15"),sQuery(id+"F2.wireOp",EDGE,"E17.filletArc"),sQuery(id+"F2.wireOp",EDGE,"E18.filletArc"),sQuery(id+"F2.wireOp",EDGE,"E19.filletArc"),sQuery(id+"F2.wireOp",EDGE,"E20.filletArc"),sQuery(id+"F13.wireOp",EDGE,"E49"),sQuery(id+"F13.wireOp",EDGE,"E50"),sQuery(id+"F13.wireOp",EDGE,"E51"),sQuery(id+"F13.wireOp",EDGE,"E52"),sQuery(id+"F13.wireOp",EDGE,"E53.filletArc"),sQuery(id+"F13.wireOp",EDGE,"E54.filletArc"),sQuery(id+"F13.wireOp",EDGE,"E55.filletArc"),sQuery(id+"F13.wireOp",EDGE,"E56.filletArc"),sQuery(id+"F23.wireOp",EDGE,"E99"),sQuery(id+"F23.wireOp",EDGE,"E100")])],"isStart":false});
            var sketch = newSketch(context, id + "F31", { "sketchPlane" : qUnion([Q0])});
            skLineSegment(sketch, "E114", {"start": v(-1.63, 28.1) * mm, "end": v(0.6, 28.1) * mm});
            skSolve(sketch);
        }
        {
            var Q0;
            Q0=makeQuery(id+"F30.opRevolve","CAP_FACE",FACE,{"disambiguationData":[OSD([makeQuery(id+"F2.imprint","IMPRINT",FACE,{"disambiguationData":[TD([[makeQuery(id+"F2.imprint","IMPRINT",EDGE,{"derivedFrom":sQuery(id+"F2.wireOp",EDGE,"E12")}),-1.0]])]})])],"isStart":false});
            var sketch = newSketch(context, id + "F32", { "sketchPlane" : qUnion([Q0])});
            skLineSegment(sketch, "E115", {"start": v(37.2, 28.12) * mm, "end": v(39.09, 28.12) * mm});
            skSolve(sketch);
        }
        {
            var Q0;
            {var subQ4=sQuery(id+"F23.wireOp",EDGE,"E99");Q0=makeQuery(id+"F31.imprint","IMPRINT",FACE,{"disambiguationData":[TD([[makeQuery(id+"F31.imprint","IMPRINT",EDGE,{"derivedFrom":makeQuery(id+"F29.opRevolve","CAP_EDGE",EDGE,{"disambiguationData":[OSD([subQ4])],"isStart":false})}),-1.0]])]});}
            var Q1;
            Q1=sQuery(id+"F31.wireOp",EDGE,"E114");
            revolve(context, id + "F33", {"operationType" : NewBodyOperationType.ADD, "entities" : qUnion([Q0]), "axis" : qUnion([Q1]), "revolveType" : RevolveType.ONE_DIRECTION, "oppositeDirection" : true, "angle" : 60 * degree});
        }
        {
            var Q0;
            {var subQ3=sQuery(id+"F2.wireOp",EDGE,"E24.filletArc");var subQ10=sQuery(id+"F2.wireOp",EDGE,"E23.filletArc");var subQ14=sQuery(id+"F2.wireOp",EDGE,"E12");Q0=makeQuery(id+"F32.imprint","IMPRINT",FACE,{"disambiguationData":[TD([[makeQuery(id+"F32.imprint","IMPRINT",EDGE,{"derivedFrom":makeQuery(id+"F30.opRevolve","CAP_EDGE",EDGE,{"disambiguationData":[OSD([subQ14,subQ10,subQ3])],"isStart":false})}),1.0]])]});}
            var Q1;
            Q1=sQuery(id+"F32.wireOp",EDGE,"E115");
            revolve(context, id + "F34", {"operationType" : NewBodyOperationType.ADD, "entities" : qUnion([Q0]), "axis" : qUnion([Q1]), "revolveType" : RevolveType.ONE_DIRECTION, "oppositeDirection" : true, "angle" : 60 * degree});
        }
    });
